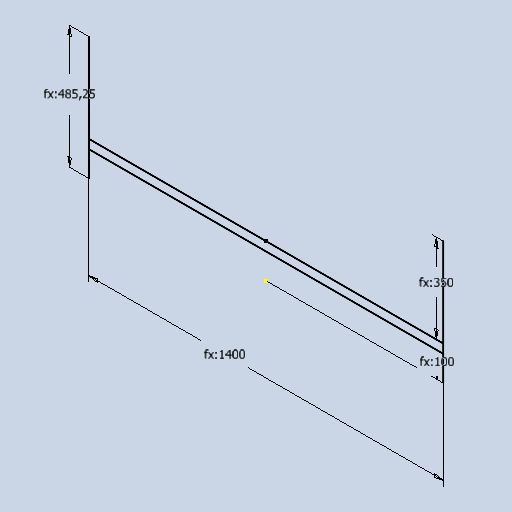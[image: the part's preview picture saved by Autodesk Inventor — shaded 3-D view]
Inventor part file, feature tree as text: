
AUTODESK INVENTOR PART (.ipt)
format: ipt  version: 2025 (Build 290162010, 162A)  size: 87,552 bytes
history: native  units: mm
features: sketch x1
ambient origin geometry x8: Origin, YZ Plane, XZ Plane, XY Plane, X Axis, Y Axis, Z Axis, Center Point
feature tree (1):
  sketch  "Sketch1"  dims[d0=485.249557mm d1=1400.0mm d2=100.0mm d4=350.0mm]
